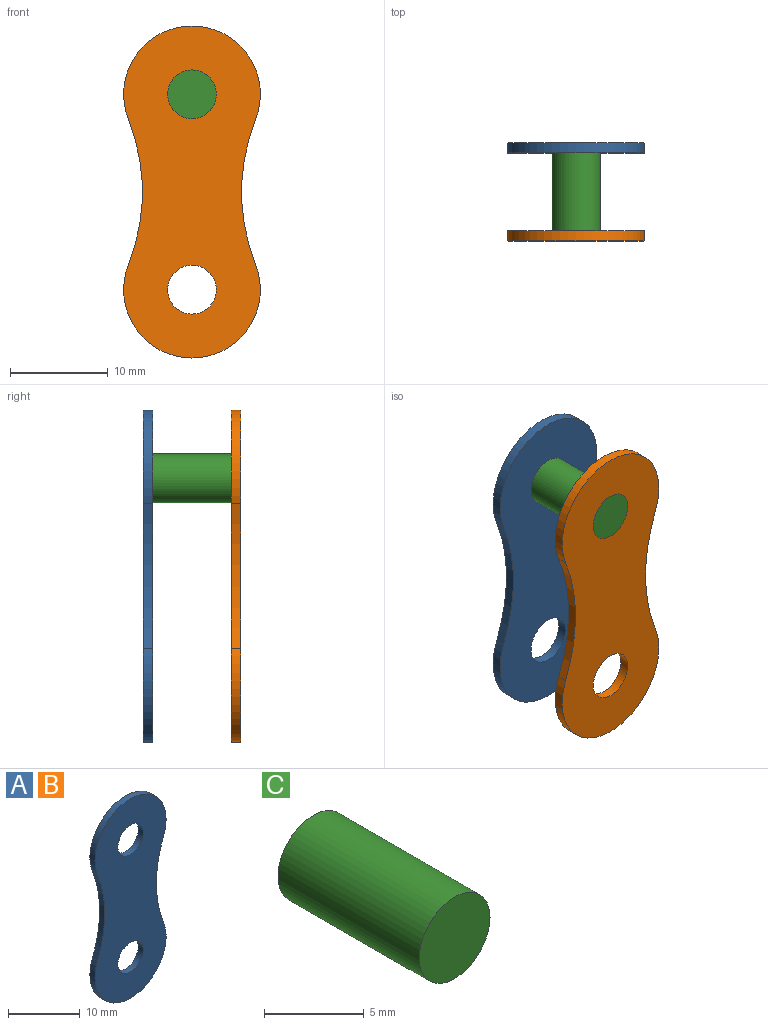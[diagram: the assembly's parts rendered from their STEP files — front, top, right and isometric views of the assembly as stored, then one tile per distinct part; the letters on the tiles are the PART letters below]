
ASSEMBLY  parts=3 mates=2
PART A: 8 faces, bbox 14x1x34 mm
  f0: cylinder r=20mm len=14.82mm, axis (0,1,0), area 15.2mm2, adj f1,f5,f6,f7
  f1: cylinder r=7mm len=14mm, axis (0,1,0), area 27.3mm2, adj f0,f2,f6,f7
  f2: cylinder r=20mm len=14.82mm, axis (0,1,0), area 15.2mm2, adj f1,f5,f6,f7
  f3: cylinder r=2.5mm len=5mm, axis (0,1,0), area 15.7mm2, adj f6,f7
  f4: cylinder r=2.5mm len=5mm, axis (0,1,0), area 15.7mm2, adj f6,f7
  f5: cylinder r=7mm len=14mm, axis (0,1,0), area 27.3mm2, adj f0,f2,f6,f7
  f6: plane 34x14mm, normal (0,-1,0), area 349.9mm2, adj f0,f1,f2,f3,f4,f5
  f7: plane 34x14mm, normal (0,1,0), area 349.9mm2, adj f0,f1,f2,f3,f4,f5
PART B: same geometry as A
PART C: 3 faces, bbox 5x10x5 mm
  f0: cylinder r=2.5mm len=10mm, axis (0,1,0), area 157.1mm2, adj f1,f2
  f1: plane 5x5mm, normal (0,-1,0), area 19.6mm2, adj f0
  f2: plane 5x5mm, normal (0,1,0), area 19.6mm2, adj f0
PLACE A t=(-11.62,-3.61,-31.32)mm
PLACE B t=(-11.62,-12.61,-31.32)mm
PLACE C t=(-29.17,-3.61,-21.12)mm
MATE fastened C.f0 <-> B.f3  axis (0,-1,0) through (-57.22,-13.61,36.9)mm
MATE fastened C.f0 <-> A.f3  axis (0,1,0) through (-57.22,-3.61,36.9)mm
